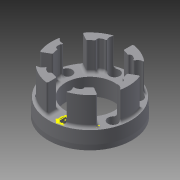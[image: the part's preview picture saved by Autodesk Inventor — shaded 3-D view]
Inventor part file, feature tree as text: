
AUTODESK INVENTOR PART (.ipt)
format: ipt  version: 2015 SP1 (Build 190203100, 203)  size: 624,128 bytes
history: native  units: in
note: dims shown in document units (in); Inventor stores cm internally (conversion verified against a paired STEP export)
features: other x3, extrude x3, fillet x3, sketch x2, chamfer x1, hole x1, pattern_circular x1
ambient origin geometry x8: Origin, YZ Plane, XZ Plane, XY Plane, X Axis, Y Axis, Z Axis, Center Point
bodies: Solid1 (feature_tree)
feature tree (14):
  other  "Wheel Insert Sketch.ipt"
  extrude  "Base"  Depth=0.3937in TaperAngle=0.0deg
  chamfer  "Chamfer2"  Distance=2.3622in Angle=360.0deg
  extrude  "Spoke"  Depth=1.0in
  hole  "Hole1"  [1 undecoded]
  fillet  "Fillet2"  Radius=0.01in
  fillet  "Fillet8"  Radius=0.1in
  pattern_circular  "Circular Pattern1"  Angle=45.0deg  [1 undecoded]
  extrude  "Center Hole"  Depth=0.02in
  fillet  "Fillet3"  Radius=0.06in
  other  "Spokes"
  other  "Circles"
  sketch  "Sketch3"  dims[d0=0.3937in d1=0.585in d2=0.0in d3=2.3622in d4=360.0deg]
  sketch  "Sketch4"  dims[d6=0.35in d7=0.0in d11=0.214in d12=0.75in d13=0.38in d14=0.05in d15=0.5635in d16=1.0in d17=0.8108in d28=1.0in d29=1.0in d30=0.0in d33=0.01in d38=0.1in d39=0.25in d40=0.015in d41=45.0deg d43=0.02in d51=0.06in]
note: 2 required parameter values undecoded (feature->parameter linkage not recoverable at this tier; creation-order binding heuristic only, values carry confidence <= 0.55)
